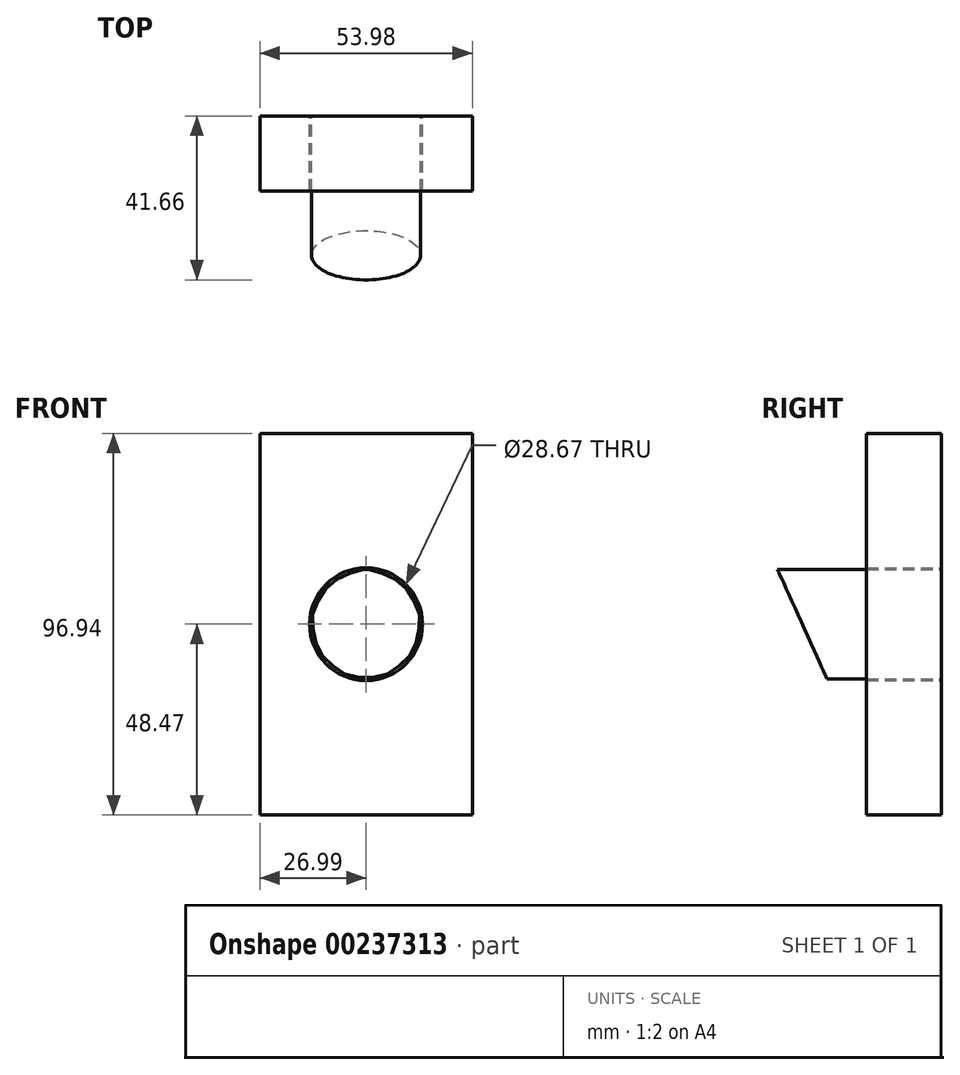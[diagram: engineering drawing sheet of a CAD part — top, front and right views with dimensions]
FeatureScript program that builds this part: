
annotation { "Feature Type Name" : "Feature", "Feature Type Description" : "" }
export const myFeature = defineFeature(function(context is Context, id is Id, definition is map)
    precondition{}
    {
        {
            var Q0;
            Q0=qCreatedBy(makeId("Front.planeOp"),FACE);
            var sketch = newSketch(context, id + "F0", { "sketchPlane" : qUnion([Q0])});
            skLineSegment(sketch, "E0.bottom", {"start": v(-26.99, 48.47) * mm, "end": v(26.99, 48.47) * mm});
            skLineSegment(sketch, "E0.top", {"start": v(-26.99, -48.47) * mm, "end": v(26.99, -48.47) * mm});
            skLineSegment(sketch, "E0.left", {"start": v(-26.99, 48.47) * mm, "end": v(-26.99, -48.47) * mm});
            skLineSegment(sketch, "E0.right", {"start": v(26.99, 48.47) * mm, "end": v(26.99, -48.47) * mm});
            skPoint(sketch, "E0.middle", {"position": v(0, 0) * mm});
            skCircle(sketch, "E1", {"center": v(0, 0) * mm, "radius": 14.34 * mm});
            skSolve(sketch);
        }
        {
            var Q0;
            Q0=makeQuery(id+"F0.imprint","IMPRINT",FACE,{"disambiguationData":[TD([[makeQuery(id+"F0.imprint","IMPRINT",EDGE,{"derivedFrom":sQuery(id+"F0.wireOp",EDGE,"E0.bottom")}),-1.0]])]});
            extrude(context, id + "F1", {"entities" : qUnion([Q0]), "depth" : 19.05 * mm});
        }
        {
            var Q0;
            Q0=qCreatedBy(makeId("Front.planeOp"),FACE);
            var sketch = newSketch(context, id + "F2", { "sketchPlane" : qUnion([Q0])});
            skCircle(sketch, "E2", {"center": v(0, 0) * mm, "radius": 13.88 * mm});
            skSolve(sketch);
        }
        {
            var Q0;
            Q0=makeQuery(id+"F2.imprint","IMPRINT",FACE,{"disambiguationData":[TD([[makeQuery(id+"F2.imprint","IMPRINT",EDGE,{"derivedFrom":sQuery(id+"F2.wireOp",EDGE,"E2")}),1.0]])]});
            extrude(context, id + "F3", {"entities" : qUnion([Q0]), "depth" : 41.66 * mm});
        }
        {
            var Q0;
            Q0=qCreatedBy(makeId("Right.planeOp"),FACE);
            var sketch = newSketch(context, id + "F4", { "sketchPlane" : qUnion([Q0])});
            skLineSegment(sketch, "E3", {"start": v(-42.43, 15.58) * mm, "end": v(-27.59, -17.23) * mm});
            skLineSegment(sketch, "E4", {"start": v(-27.59, -17.23) * mm, "end": v(-42.07, -17.23) * mm});
            skLineSegment(sketch, "E5", {"start": v(-42.07, -17.23) * mm, "end": v(-42.43, 15.58) * mm});
            skSolve(sketch);
        }
        {
            var Q0;
            Q0=makeQuery(id+"F4.imprint","IMPRINT",FACE,{"disambiguationData":[TD([[makeQuery(id+"F4.imprint","IMPRINT",EDGE,{"derivedFrom":sQuery(id+"F4.wireOp",EDGE,"E3")}),-1.0]])]});
            extrude(context, id + "F5", {"entities" : qUnion([Q0]), "operationType" : NewBodyOperationType.REMOVE, "oppositeDirection" : true, "depth" : 25.4 * mm, "hasSecondDirection" : true, "secondDirectionOppositeDirection" : false, "secondDirectionDepth" : 25.4 * mm});
        }
    });
